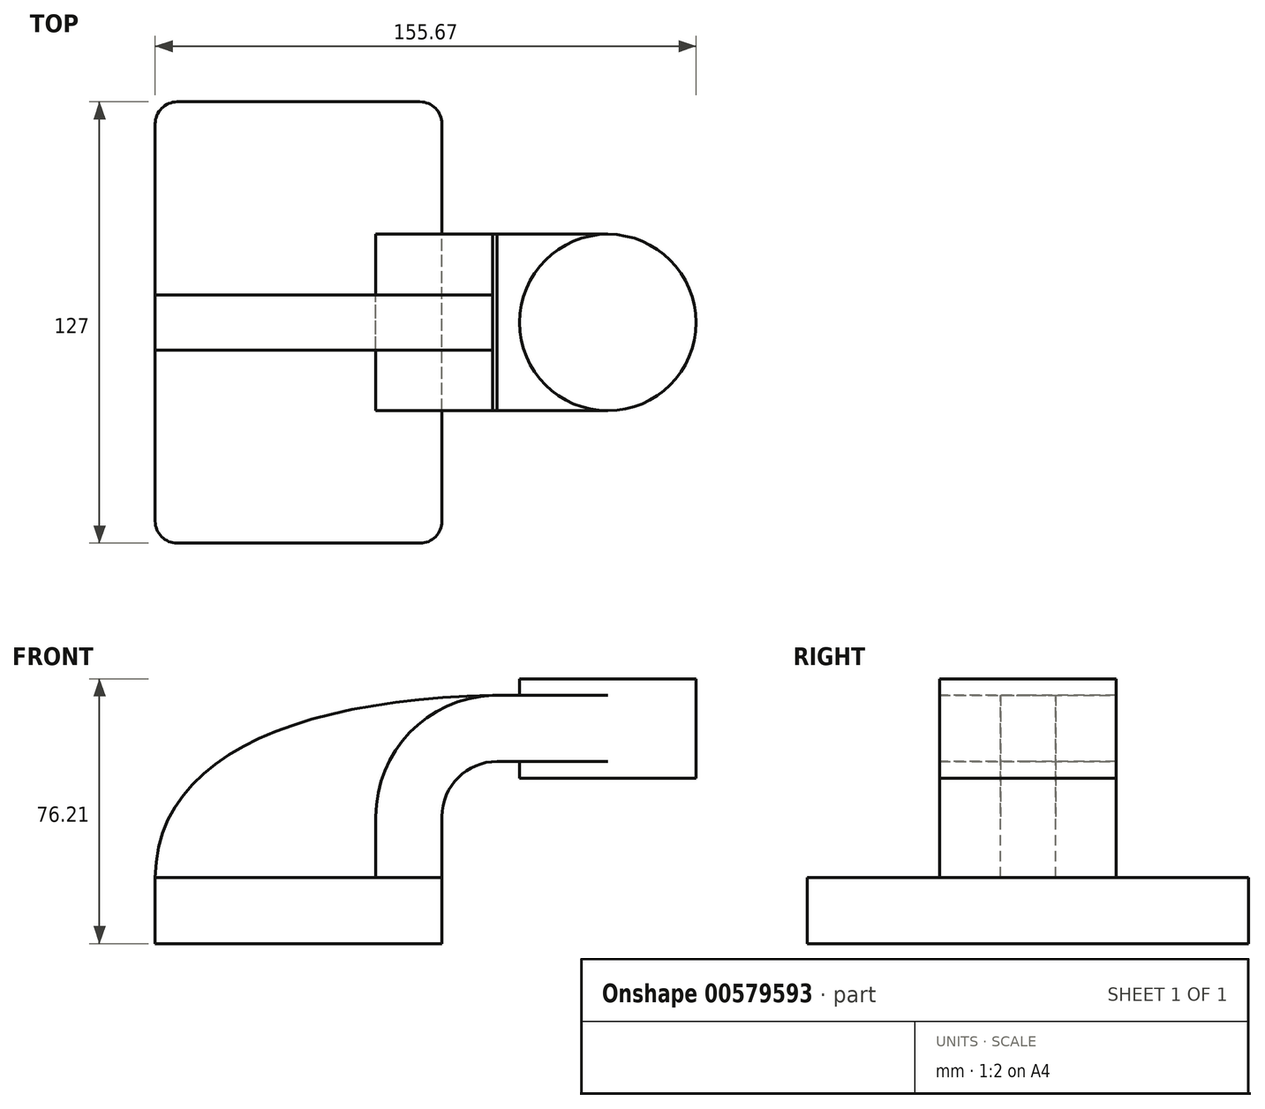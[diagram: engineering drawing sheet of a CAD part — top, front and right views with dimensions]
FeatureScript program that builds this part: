
annotation { "Feature Type Name" : "Feature", "Feature Type Description" : "" }
export const myFeature = defineFeature(function(context is Context, id is Id, definition is map)
    precondition{}
    {
        {
            var Q0;
            Q0=qCreatedBy(makeId("Front.planeOp"),FACE);
            var sketch = newSketch(context, id + "F0", { "sketchPlane" : qUnion([Q0])});
            skLineSegment(sketch, "E0.bottom", {"start": v(41.28, -9.52) * mm, "end": v(-41.28, -9.53) * mm});
            skLineSegment(sketch, "E0.top", {"start": v(41.28, 9.53) * mm, "end": v(-41.28, 9.53) * mm});
            skLineSegment(sketch, "E0.left", {"start": v(41.28, -9.52) * mm, "end": v(41.28, 9.53) * mm});
            skLineSegment(sketch, "E0.right", {"start": v(-41.28, -9.53) * mm, "end": v(-41.28, 9.53) * mm});
            skPoint(sketch, "E0.middle", {"position": v(0, 0) * mm});
            skLineSegment(sketch, "E1.bottom", {"start": v(114.39, 38.1) * mm, "end": v(63.59, 38.1) * mm});
            skLineSegment(sketch, "E1.top", {"start": v(114.39, 66.68) * mm, "end": v(63.59, 66.68) * mm});
            skLineSegment(sketch, "E1.left", {"start": v(114.39, 38.1) * mm, "end": v(114.39, 66.68) * mm});
            skLineSegment(sketch, "E1.right", {"start": v(63.59, 38.1) * mm, "end": v(63.59, 66.68) * mm});
            skPoint(sketch, "E1.middle", {"position": v(88.99, 52.39) * mm});
            skLineSegment(sketch, "E2", {"start": v(41.28, 9.53) * mm, "end": v(41.28, 27) * mm});
            skArc(sketch, "E3", {"start": v(41.27, 27) * mm, "mid": v(45.92, 38.23) * mm, "end": v(57.15, 42.88) * mm});
            skLineSegment(sketch, "E4", {"start": v(57.15, 42.88) * mm, "end": v(88.99, 42.88) * mm});
            skLineSegment(sketch, "E5.0", {"start": v(57.15, 61.93) * mm, "end": v(88.99, 61.93) * mm});
            skArc(sketch, "E5.1", {"start": v(22.23, 27) * mm, "mid": v(32.45, 51.7) * mm, "end": v(57.15, 61.93) * mm});
            skLineSegment(sketch, "E5.2", {"start": v(22.22, 9.53) * mm, "end": v(22.22, 27) * mm});
            skLineSegment(sketch, "E6", {"start": v(88.99, 38.1) * mm, "end": v(88.99, 66.68) * mm});
            skFitSpline(sketch, "E7", {"points": [v(-41.28, 9.53) * mm, v(57.15, 61.93) * mm], "startDerivative": vector(1.16, 105.54) * mm, "endDerivative": vector(171.45, 2.98) * mm});
            skSolve(sketch);
        }
        {
            var Q0;
            Q0=makeQuery(id+"F0.imprint","IMPRINT",FACE,{"disambiguationData":[TD([[makeQuery(id+"F0.imprint","IMPRINT",EDGE,{"derivedFrom":sQuery(id+"F0.wireOp",EDGE,"E0.bottom")}),-1.0]])]});
            extrude(context, id + "F1", {"entities" : qUnion([Q0]), "endBound" : BoundingType.SYMMETRIC, "depth" : 127 * mm, "offsetDistance" : 25.4 * mm});
        }
        {
            var Q0;
            {var subQ1=sQuery(id+"F0.wireOp",EDGE,"E2");Q0=makeQuery(id+"F0.imprint","IMPRINT",FACE,{"disambiguationData":[TD([[makeQuery(id+"F0.imprint","IMPRINT",EDGE,{"derivedFrom":subQ1}),1.0]])]});}
            var Q1;
            {var subQ0=sQuery(id+"F0.wireOp",EDGE,"E4");var subQ1=sQuery(id+"F0.wireOp",EDGE,"E1.right");var subQ2=makeQuery(id+"F0.imprint","INTERSECT",VERTEX,{"derivedFrom":[subQ1,subQ0]});Q1=makeQuery(id+"F0.imprint","IMPRINT",FACE,{"disambiguationData":[TD([[makeQuery(id+"F0.imprint","IMPRINT",EDGE,{"disambiguationData":[TD([[subQ2,-1.0]])],"derivedFrom":subQ1}),-1.0]])]});}
            extrude(context, id + "F2", {"entities" : qUnion([Q0, Q1]), "endBound" : BoundingType.SYMMETRIC, "depth" : 50.8 * mm, "offsetDistance" : 25.4 * mm});
        }
        {
            var Q0;
            {var subQ3=sQuery(id+"F0.wireOp",EDGE,"E5.2");Q0=makeQuery(id+"F0.imprint","IMPRINT",FACE,{"disambiguationData":[TD([[makeQuery(id+"F0.imprint","IMPRINT",EDGE,{"derivedFrom":subQ3}),1.0]])]});}
            extrude(context, id + "F3", {"entities" : qUnion([Q0]), "endBound" : BoundingType.SYMMETRIC, "depth" : 15.88 * mm, "offsetDistance" : 25.4 * mm});
        }
        {
            var Q0;
            {var subQ0=sQuery(id+"F0.wireOp",EDGE,"E1.left");Q0=makeQuery(id+"F0.imprint","IMPRINT",FACE,{"disambiguationData":[TD([[makeQuery(id+"F0.imprint","IMPRINT",EDGE,{"derivedFrom":subQ0}),1.0]])]});}
            var Q1;
            Q1=sQuery(id+"F0.wireOp",EDGE,"E6");
            revolve(context, id + "F4", {"operationType" : NewBodyOperationType.ADD, "entities" : qUnion([Q0]), "axis" : qUnion([Q1]), "revolveType" : RevolveType.FULL});
        }
        {
            var Q0;
            Q0=makeQuery(id+"F1.opExtrude","CAP_EDGE",EDGE,{"disambiguationData":[OSD([sQuery(id+"F0.wireOp",EDGE,"E0.right")])],"isStart":false});
            var Q1;
            Q1=makeQuery(id+"F1.opExtrude","CAP_EDGE",EDGE,{"disambiguationData":[OSD([sQuery(id+"F0.wireOp",EDGE,"E0.left")])],"isStart":false});
            var Q2;
            Q2=makeQuery(id+"F1.opExtrude","CAP_EDGE",EDGE,{"disambiguationData":[OSD([sQuery(id+"F0.wireOp",EDGE,"E0.left")])],"isStart":true});
            var Q3;
            Q3=makeQuery(id+"F1.opExtrude","CAP_EDGE",EDGE,{"disambiguationData":[OSD([sQuery(id+"F0.wireOp",EDGE,"E0.right")])],"isStart":true});
            fillet(context, id + "F5", {"entities" : qUnion([Q0, Q1, Q2, Q3]), "radius" : 6.35 * mm, "tangentPropagation" : true, "allowEdgeOverflow" : false});
        }
    });
